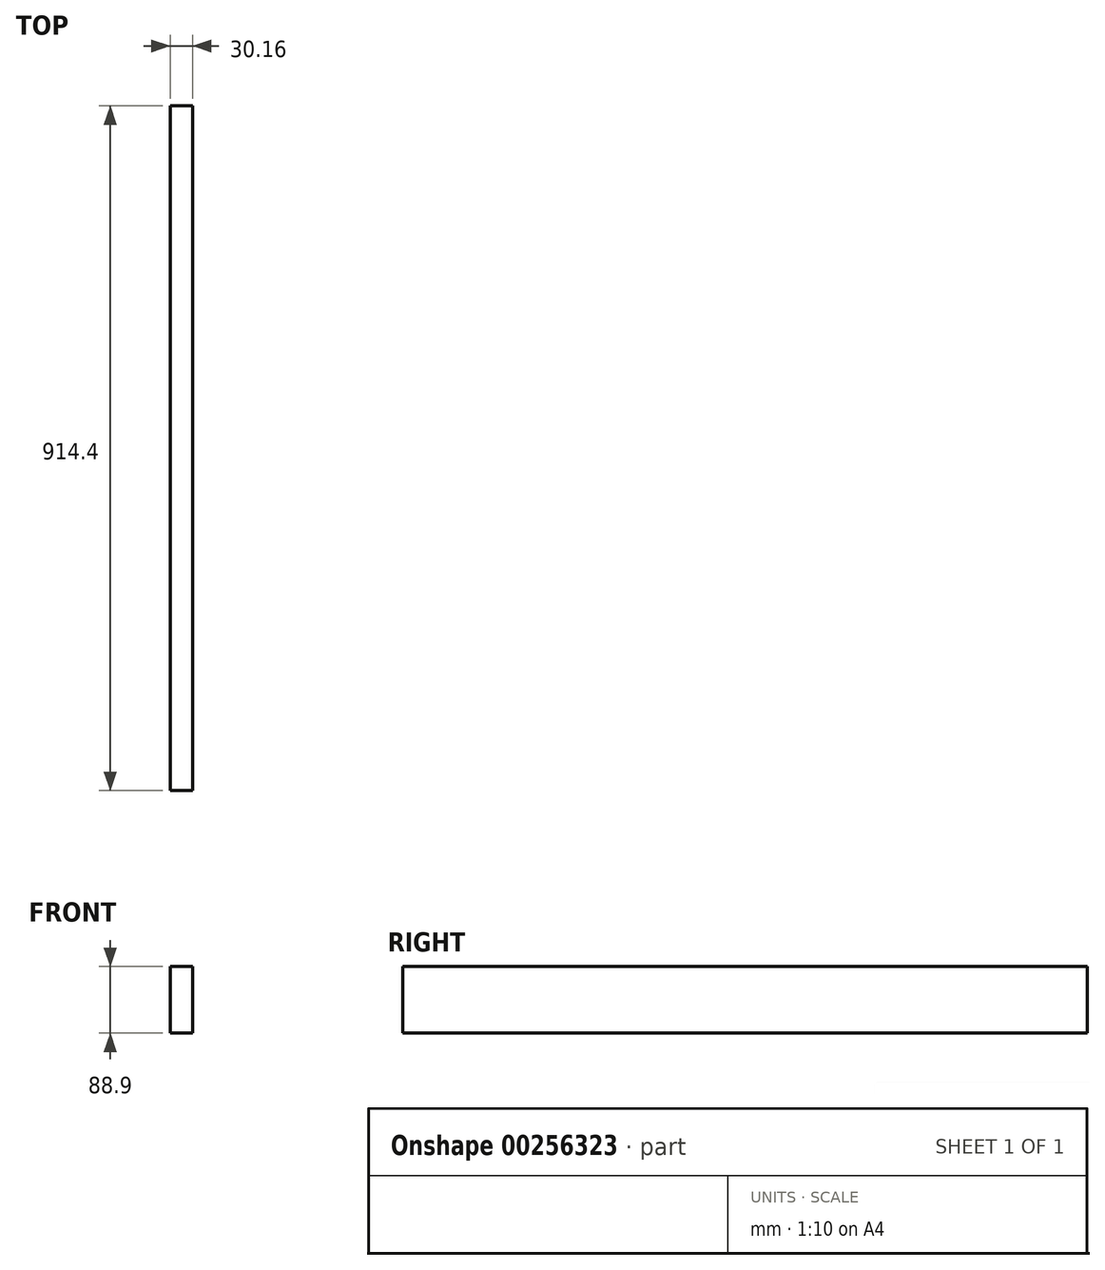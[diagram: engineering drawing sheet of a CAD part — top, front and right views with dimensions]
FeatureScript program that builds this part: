
annotation { "Feature Type Name" : "Feature", "Feature Type Description" : "" }
export const myFeature = defineFeature(function(context is Context, id is Id, definition is map)
    precondition{}
    {
        {
            var Q0;
            Q0=qCreatedBy(makeId("Front.planeOp"),FACE);
            var sketch = newSketch(context, id + "F0", { "sketchPlane" : qUnion([Q0])});
            skLineSegment(sketch, "E0.bottom", {"start": v(-15.08, 44.45) * mm, "end": v(15.08, 44.45) * mm});
            skLineSegment(sketch, "E0.top", {"start": v(-15.08, -44.45) * mm, "end": v(15.08, -44.45) * mm});
            skLineSegment(sketch, "E0.left", {"start": v(-15.08, 44.45) * mm, "end": v(-15.08, -44.45) * mm});
            skLineSegment(sketch, "E0.right", {"start": v(15.08, 44.45) * mm, "end": v(15.08, -44.45) * mm});
            skSolve(sketch);
        }
        {
            var Q0;
            Q0=qSketchRegion(id+"F0",true);
            extrude(context, id + "F1", {"entities" : qUnion([Q0]), "endBound" : BoundingType.SYMMETRIC, "depth" : 914.4 * mm});
        }
    });
